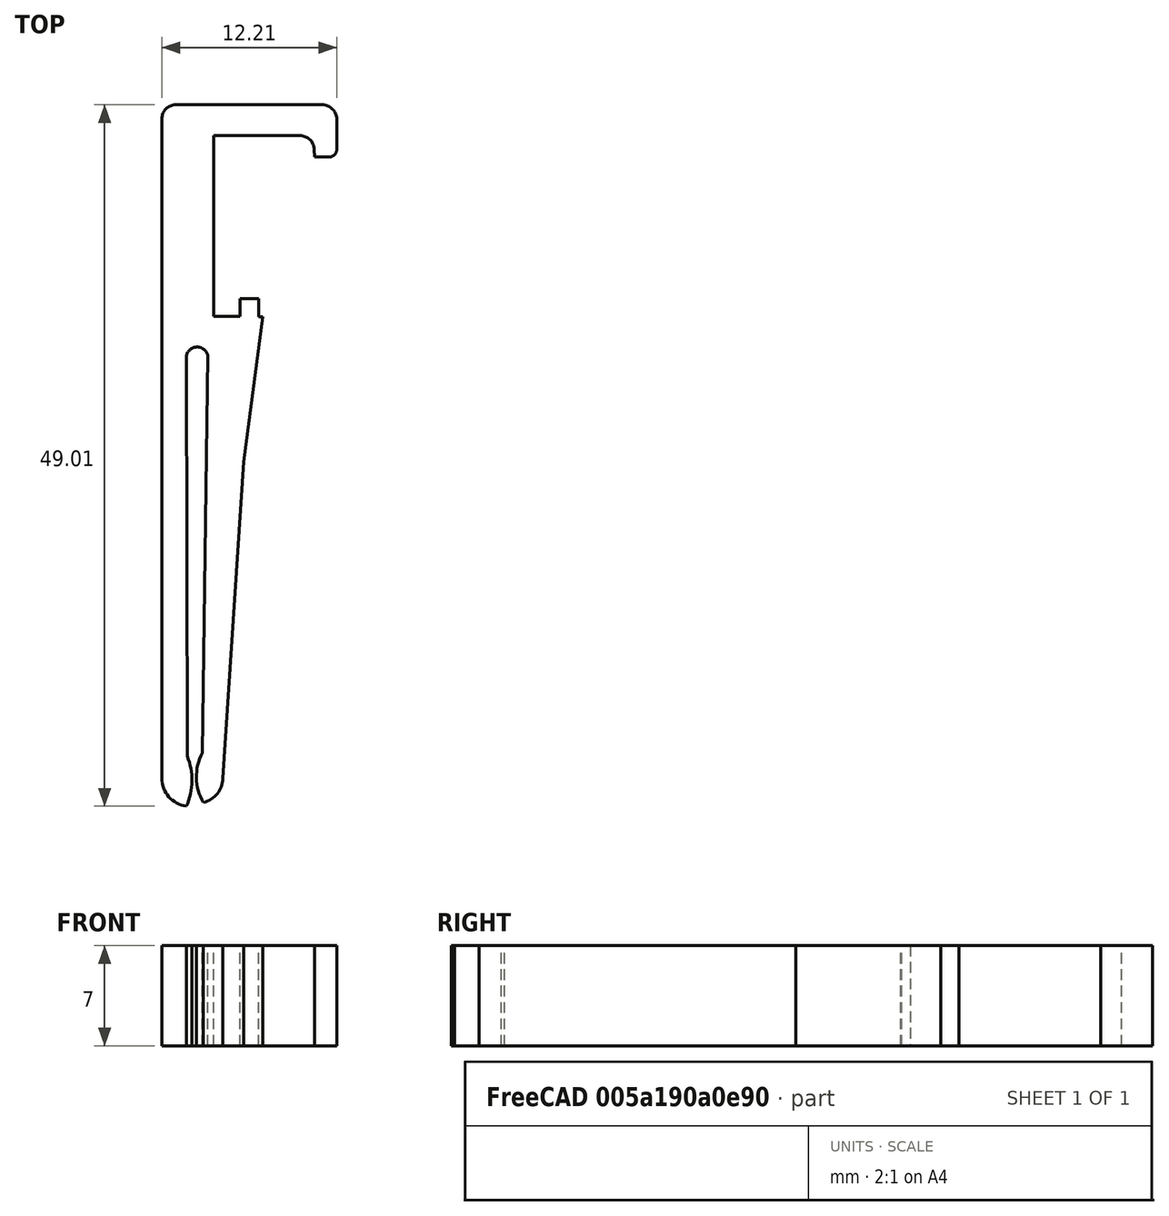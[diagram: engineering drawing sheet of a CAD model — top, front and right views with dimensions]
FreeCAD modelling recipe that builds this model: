
FCSTD DOCUMENT  (FreeCAD 0.15R4503 (Git))
Label: jarv_clip
License: CC-BY 3.0
LicenseURL: http://creativecommons.org/licenses/by/3.0/
objects: PartDesign::Fillet×3, Sketcher::SketchObject×1, PartDesign::Pad×1
note: 6 computed .brp shape members not serialized (recipe doc carries the construction recipe); baked Part::Feature solids carry a one-line shape summary decoded from their .brp

FEATURE [Sketcher::SketchObject] Sketch
  sketch-geometry (23):
    g0: LineSegment StartX=1.14035 StartY=38.2119 StartZ=0 EndX=6.60848 EndY=38.2119 EndZ=0
    g1: LineSegment StartX=0.178586 StartY=37.2501 StartZ=0 EndX=0.177781 EndY=-8.83959 EndZ=0
    g2: LineSegment StartX=4.44403 StartY=-8.84578 StartZ=0 EndX=5.87844 EndY=13.2727 EndZ=0
    g3: ArcOfCircle CenterX=2.64919 CenterY=-8.80762 CenterZ=0 NormalX=0 NormalY=0 NormalZ=1 Radius=1.79524 StartAngle=4.9516 EndAngle=6.26193
    g4: ArcOfCircle CenterX=2.1221 CenterY=-8.87139 CenterZ=0 NormalX=0 NormalY=0 NormalZ=1 Radius=1.94458 StartAngle=3.12524 EndAngle=4.59574
    g5: ArcOfCircle CenterX=1.14035 CenterY=37.2501 CenterZ=0 NormalX=0 NormalY=0 NormalZ=1 Radius=0.961767 StartAngle=1.5708 EndAngle=3.14159
    g6: ArcOfCircle CenterX=2.64039 CenterY=20.5192 CenterZ=0 NormalX=0 NormalY=0 NormalZ=1 Radius=0.766349 StartAngle=0.184766 EndAngle=3.00904
    g7: LineSegment StartX=1.88076 StartY=20.6204 StartZ=0 EndX=1.95218 EndY=-7.31354 EndZ=0
    g8: LineSegment StartX=3.39369 StartY=20.6599 StartZ=0 EndX=2.99206 EndY=-7.06815 EndZ=0
    g9: ArcOfCircle CenterX=-2.2067 CenterY=-8.99139 CenterZ=0 NormalX=0 NormalY=0 NormalZ=1 Radius=4.48458 StartAngle=5.8674 EndAngle=6.66665
    g10: ArcOfCircle CenterX=6.2181 CenterY=-8.73454 CenterZ=0 NormalX=0 NormalY=0 NormalZ=1 Radius=3.63101 StartAngle=2.6648 EndAngle=3.66573
    g11: LineSegment StartX=3.79207 StartY=23.4374 StartZ=0 EndX=5.64769 EndY=23.4374 EndZ=0
    g12: LineSegment StartX=5.64769 StartY=23.4374 StartZ=0 EndX=5.64769 EndY=24.6744 EndZ=0
    g13: LineSegment StartX=5.64769 StartY=24.6744 StartZ=0 EndX=6.94662 EndY=24.6744 EndZ=0
    g14: LineSegment StartX=6.94662 StartY=24.6744 StartZ=0 EndX=6.94662 EndY=23.3943 EndZ=0
    g15: LineSegment StartX=3.79207 StartY=23.4374 StartZ=0 EndX=3.79207 EndY=36.0555 EndZ=0
    g16: LineSegment StartX=3.79207 StartY=36.0555 StartZ=0 EndX=10.7816 EndY=36.0555 EndZ=0
    g17: LineSegment StartX=10.7816 StartY=36.0555 StartZ=0 EndX=10.8434 EndY=34.5711 EndZ=0
    g18: LineSegment StartX=10.8434 StartY=34.5711 StartZ=0 EndX=12.3898 EndY=34.5711 EndZ=0
    g19: LineSegment StartX=12.3898 StartY=34.5711 StartZ=0 EndX=12.3898 EndY=38.2119 EndZ=0
    g20: LineSegment StartX=12.3898 StartY=38.2119 StartZ=0 EndX=6.60848 EndY=38.2119 EndZ=0
    g21: LineSegment StartX=6.94662 StartY=23.3943 StartZ=0 EndX=7.23093 EndY=23.3943 EndZ=0
    g22: LineSegment StartX=7.23093 StartY=23.3943 StartZ=0 EndX=5.87844 EndY=13.2727 EndZ=0
  constraints (28):
    c: Coincident(g7,g6)
    c: Coincident(g8,g6)
    c: Coincident(g9,g4)
    c: Coincident(g10,g3)
    c: Horizontal(g11)
    c: Coincident(g11,g12)
    c: Coincident(g13,g14)
    c: Vertical(g14)
    c: Vertical(g15)
    c: Coincident(g15,g16)
    c: Horizontal(g16)
    c: Coincident(g16,g17)
    c: Coincident(g17,g18)
    c: Horizontal(g18)
    c: Coincident(g18,g19)
    c: Vertical(g19)
    c: Coincident(g19,g20)
    c: Coincident(g20,g0)
    c: Horizontal(g20)
    c: Coincident(g11,g15)
    c: Coincident(g14,g21)
    c: Horizontal(g21)
    c: Coincident(g21,g22)
    c: Coincident(g22,g2)
    c: Coincident(g8,g10)
    c: Coincident(g7,g9)
    c: Coincident(g2,g3)
    c: Coincident(g1,g4)
FEATURE [PartDesign::Pad] Pad
  Length = 7
  Length2 = 100
  Sketch = -> Sketch
  Type = 0
FEATURE [PartDesign::Fillet] Fillet
  Base = -> Pad [Edge11]
  Radius = 0.5
FEATURE [PartDesign::Fillet] Fillet001
  Base = -> Fillet [Edge3]
  Radius = 1
FEATURE [PartDesign::Fillet] Fillet002
  Base = -> Fillet001 [Edge58]
  Radius = 1
